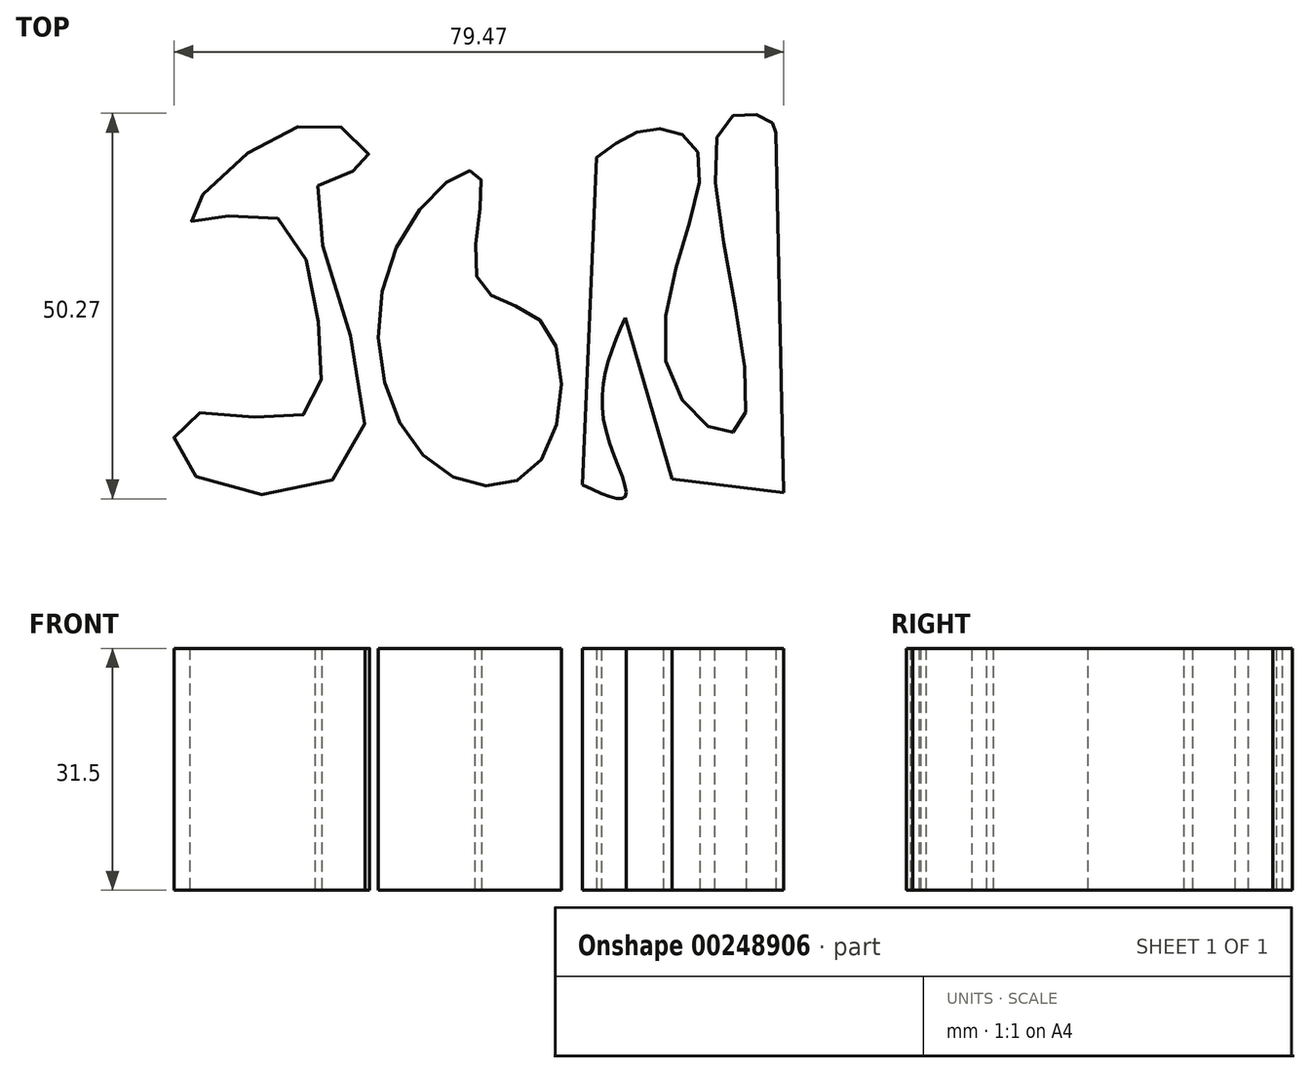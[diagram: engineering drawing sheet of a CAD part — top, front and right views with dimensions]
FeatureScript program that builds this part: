
annotation { "Feature Type Name" : "Feature", "Feature Type Description" : "" }
export const myFeature = defineFeature(function(context is Context, id is Id, definition is map)
    precondition{}
    {
        {
            var Q0;
            Q0=qCreatedBy(makeId("Top.planeOp"),FACE);
            var sketch = newSketch(context, id + "F0", { "sketchPlane" : qUnion([Q0])});
            skLineSegment(sketch, "E0", {"start": v(-42.06, 48.76) * mm, "end": v(-3.66, 48.76) * mm});
            skLineSegment(sketch, "E1", {"start": v(48.67, 48.76) * mm, "end": v(48.67, -7.42) * mm});
            skLineSegment(sketch, "E2", {"start": v(48.67, -7.42) * mm, "end": v(-42.06, -7.42) * mm});
            skLineSegment(sketch, "E3", {"start": v(-42.06, -7.42) * mm, "end": v(-42.06, 48.76) * mm});
            skFitSpline(sketch, "E4", {"points": [v(-20.9, 34.95) * mm, v(-15.71, 0.05) * mm, v(-37.6, -2.31) * mm, v(-37.93, 4.89) * mm, v(-23.24, 4.89) * mm, v(-20.75, 16.14) * mm, v(-27.3, 31.18) * mm, v(-37.5, 30.4) * mm, v(-29.78, 39.42) * mm, v(-17.32, 42.33) * mm, v(-14.44, 37.54) * mm, v(-20.9, 34.95) * mm]});
            skPoint(sketch, "E5", {"position": v(-19.79, 25.42) * mm});
            skFitSpline(sketch, "E6", {"points": [v(-10.73, 26.87) * mm, v(0, 36.53) * mm, v(0, 22.55) * mm, v(8.7, 16.74) * mm, v(7.1, -2.07) * mm, v(-7.4, 0) * mm, v(-10.73, 26.87) * mm]});
            skLineSegment(sketch, "E7", {"start": v(13.53, -4.03) * mm, "end": v(15.4, 38.64) * mm});
            skFitSpline(sketch, "E8", {"points": [v(15.4, 38.64) * mm, v(22.66, 42.38) * mm, v(28.79, 38.64) * mm, v(24.63, 11.13) * mm, v(34.19, 3.55) * mm, v(31.6, 42.58) * mm, v(37.92, 43.52) * mm, v(38.75, 41.86) * mm], "startDerivative": vector(58.3, 44.73) * mm, "endDerivative": vector(3.16, -30.8) * mm});
            skLineSegment(sketch, "E9", {"start": v(38.75, 41.86) * mm, "end": v(39.8, -5.07) * mm});
            skLineSegment(sketch, "E10", {"start": v(39.8, -5.07) * mm, "end": v(25.26, -3.3) * mm});
            skLineSegment(sketch, "E11", {"start": v(25.26, -3.3) * mm, "end": v(19.13, 17.77) * mm});
            skFitSpline(sketch, "E12", {"points": [v(19.13, 17.77) * mm, v(16.33, 4.38) * mm, v(19.13, -5.58) * mm, v(13.53, -4.03) * mm], "startDerivative": vector(-13.86, -32.31) * mm, "endDerivative": vector(-29.33, 13.77) * mm});
            skFitSpline(sketch, "E13", {"points": [v(-3.66, 48.76) * mm, v(6.38, 57.84) * mm, v(16.3, 48.76) * mm], "startDerivative": vector(22, 13.72) * mm, "endDerivative": vector(17.86, -14.16) * mm});
            skLineSegment(sketch, "E14.trimOffspring", {"start": v(16.3, 48.76) * mm, "end": v(48.67, 48.76) * mm});
            skFitSpline(sketch, "E15", {"points": [v(2.42, 49.64) * mm, v(6.15, 53.28) * mm, v(10.66, 50.52) * mm, v(9.37, 46.84) * mm, v(4.33, 46.15) * mm, v(2.42, 49.64) * mm]});
            skSolve(sketch);
        }
        {
            var Q0;
            Q0=makeQuery(id+"F0.imprint","IMPRINT",FACE,{"disambiguationData":[TD([[makeQuery(id+"F0.imprint","IMPRINT",EDGE,{"derivedFrom":sQuery(id+"F0.wireOp",EDGE,"E6")}),-1.0]])]});
            var Q1;
            Q1=makeQuery(id+"F0.imprint","IMPRINT",FACE,{"disambiguationData":[TD([[makeQuery(id+"F0.imprint","IMPRINT",EDGE,{"derivedFrom":sQuery(id+"F0.wireOp",EDGE,"E7")}),-1.0]])]});
            var Q2;
            Q2=makeQuery(id+"F0.imprint","IMPRINT",FACE,{"disambiguationData":[TD([[makeQuery(id+"F0.imprint","IMPRINT",EDGE,{"derivedFrom":sQuery(id+"F0.wireOp",EDGE,"E4")}),-1.0]])]});
            extrude(context, id + "F1", {"entities" : qUnion([Q0, Q1, Q2]), "depth" : 31.5 * mm});
        }
    });
